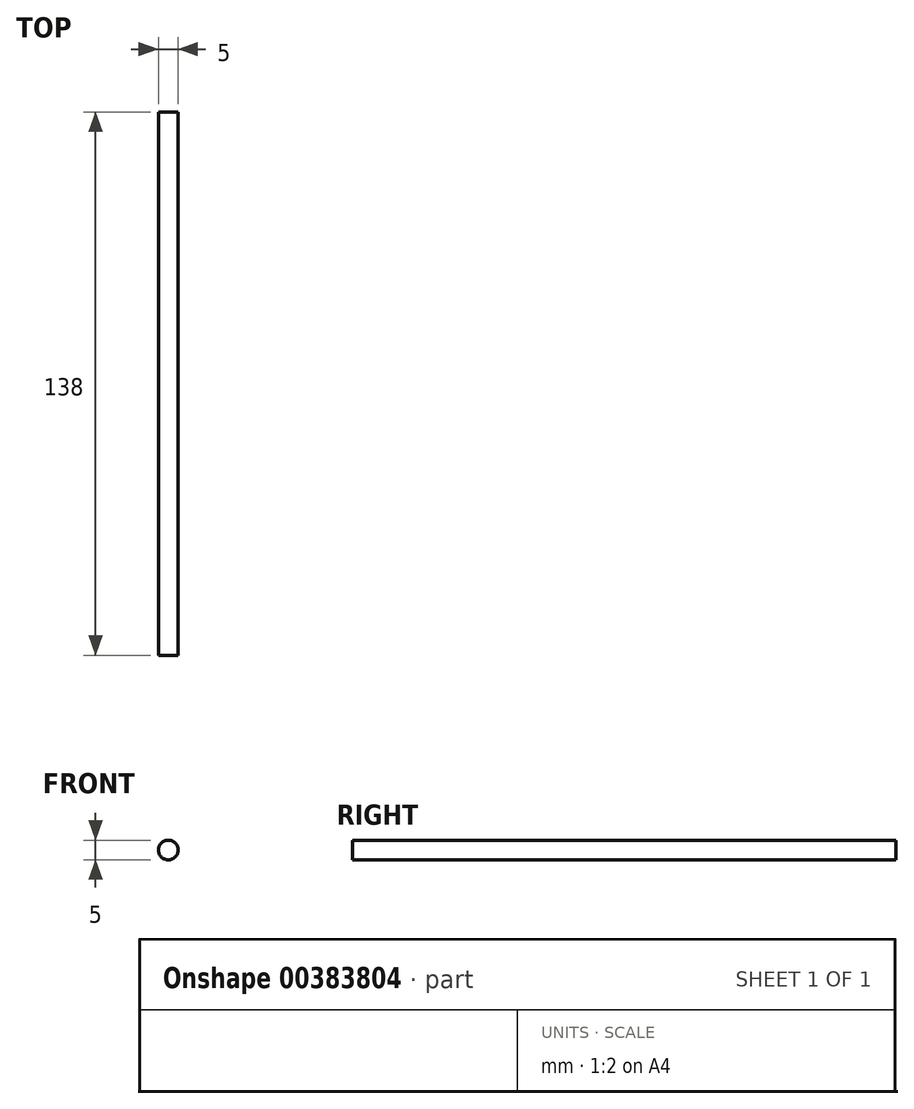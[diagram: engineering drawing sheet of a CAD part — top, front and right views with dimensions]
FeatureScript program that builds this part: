
annotation { "Feature Type Name" : "Feature", "Feature Type Description" : "" }
export const myFeature = defineFeature(function(context is Context, id is Id, definition is map)
    precondition{}
    {
        {
            var Q0;
            Q0=qCreatedBy(makeId("Front.planeOp"),FACE);
            var sketch = newSketch(context, id + "F0", { "sketchPlane" : qUnion([Q0])});
            skCircle(sketch, "E0", {"center": v(0, 0) * mm, "radius": 2.5 * mm});
            skSolve(sketch);
        }
        {
            var Q0;
            Q0 = qSketchRegion(id + "F0", true);
            extrude(context, id + "F1", {"entities" : qUnion([Q0]), "depth" : 138 * mm});
        }
    });
